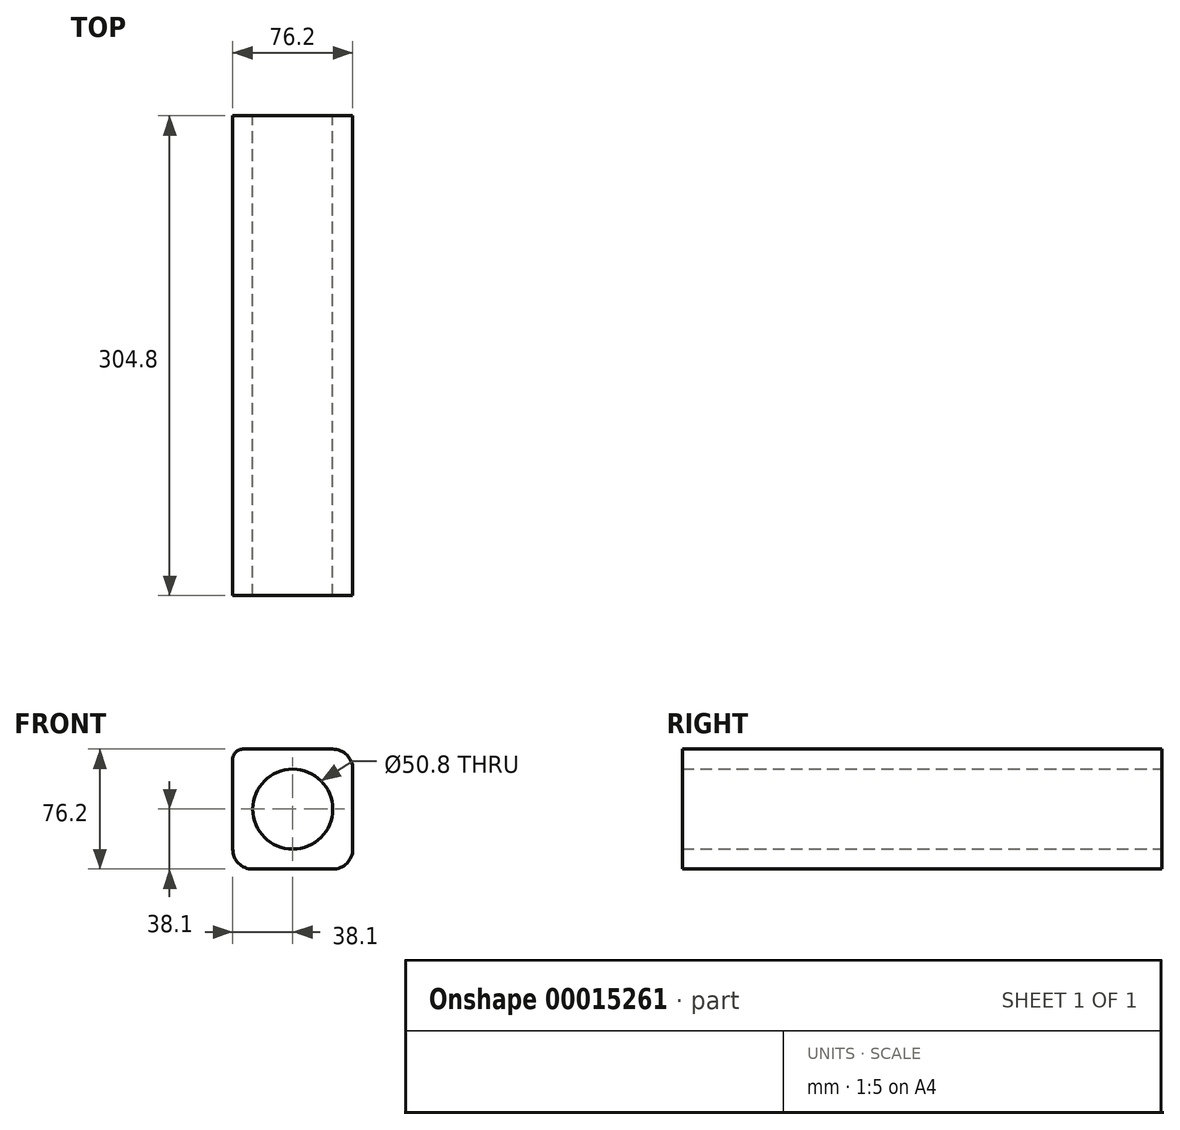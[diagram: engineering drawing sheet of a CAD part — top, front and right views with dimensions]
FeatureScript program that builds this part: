
annotation { "Feature Type Name" : "Feature", "Feature Type Description" : "" }
export const myFeature = defineFeature(function(context is Context, id is Id, definition is map)
    precondition{}
    {
        {
            var Q0;
            Q0=qCreatedBy(makeId("Front.planeOp"),FACE);
            var sketch = newSketch(context, id + "F0", { "sketchPlane" : qUnion([Q0])});
            skLineSegment(sketch, "E0.bottom", {"start": v(-31.75, 38.1) * mm, "end": v(25.4, 38.1) * mm});
            skLineSegment(sketch, "E0.top", {"start": v(-25.4, -38.1) * mm, "end": v(25.4, -38.1) * mm});
            skLineSegment(sketch, "E0.left", {"start": v(-38.1, 31.75) * mm, "end": v(-38.1, -25.4) * mm});
            skLineSegment(sketch, "E0.right", {"start": v(38.1, 25.4) * mm, "end": v(38.1, -25.4) * mm});
            skCircle(sketch, "E1", {"center": v(0, 0) * mm, "radius": 25.4 * mm});
            skPoint(sketch, "E2.visualSharp", {"position": v(-38.1, 38.1) * mm});
            skArc(sketch, "E2.filletArc", {"start": v(-31.75, 38.1) * mm, "mid": v(-36.24, 36.24) * mm, "end": v(-38.1, 31.75) * mm});
            skPoint(sketch, "E3.visualSharp", {"position": v(-38.1, -38.1) * mm});
            skArc(sketch, "E3.filletArc", {"start": v(-38.1, -25.4) * mm, "mid": v(-34.38, -34.38) * mm, "end": v(-25.4, -38.1) * mm});
            skPoint(sketch, "E4.visualSharp", {"position": v(38.1, -38.1) * mm});
            skArc(sketch, "E4.filletArc", {"start": v(25.4, -38.1) * mm, "mid": v(34.38, -34.38) * mm, "end": v(38.1, -25.4) * mm});
            skPoint(sketch, "E5.visualSharp", {"position": v(38.1, 38.1) * mm});
            skArc(sketch, "E5.filletArc", {"start": v(38.1, 25.4) * mm, "mid": v(34.38, 34.38) * mm, "end": v(25.4, 38.1) * mm});
            skSolve(sketch);
        }
        {
            var Q0;
            Q0=makeQuery(id+"F0.imprint","IMPRINT",FACE,{"disambiguationData":[TD([[makeQuery(id+"F0.imprint","IMPRINT",EDGE,{"derivedFrom":sQuery(id+"F0.wireOp",EDGE,"E0.bottom")}),-1.0]])]});
            extrude(context, id + "F1", {"entities" : qUnion([Q0]), "endBound" : BoundingType.SYMMETRIC, "depth" : 304.8 * mm});
        }
    });
